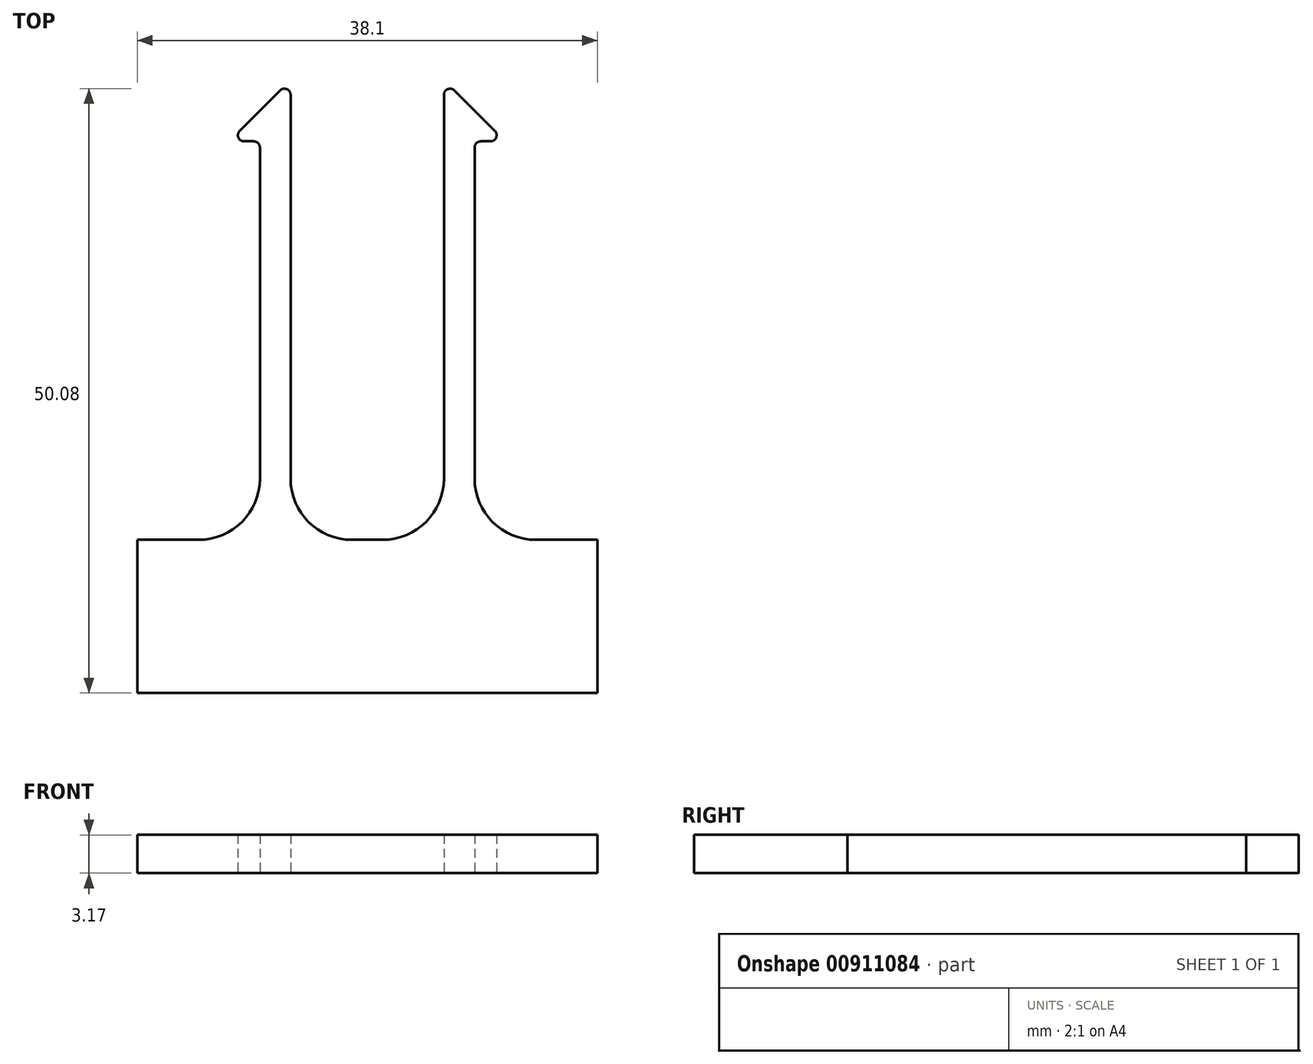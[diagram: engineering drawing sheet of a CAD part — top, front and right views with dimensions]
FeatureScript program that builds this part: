
annotation { "Feature Type Name" : "Feature", "Feature Type Description" : "" }
export const myFeature = defineFeature(function(context is Context, id is Id, definition is map)
    precondition{}
    {
        {
            var Q0;
            Q0=qCreatedBy(makeId("Top.planeOp"),FACE);
            var sketch = newSketch(context, id + "F0", { "sketchPlane" : qUnion([Q0])});
            skLineSegment(sketch, "E0.bottom", {"start": v(0, 0) * mm, "end": v(38.1, 0) * mm});
            skLineSegment(sketch, "E0.top", {"start": v(0, 50.8) * mm, "end": v(38.1, 50.8) * mm});
            skLineSegment(sketch, "E0.left", {"start": v(0, 0) * mm, "end": v(0, 50.8) * mm});
            skLineSegment(sketch, "E0.right", {"start": v(38.1, 0) * mm, "end": v(38.1, 50.8) * mm});
            skLineSegment(sketch, "E1", {"start": v(12.7, 50.8) * mm, "end": v(12.7, 12.7) * mm});
            skLineSegment(sketch, "E2", {"start": v(12.7, 12.7) * mm, "end": v(25.4, 12.7) * mm});
            skLineSegment(sketch, "E3", {"start": v(25.4, 12.7) * mm, "end": v(25.4, 50.8) * mm});
            skLineSegment(sketch, "E4", {"start": v(12.7, 50.8) * mm, "end": v(7.62, 45.72) * mm});
            skLineSegment(sketch, "E5", {"start": v(7.62, 45.72) * mm, "end": v(10.16, 45.72) * mm});
            skLineSegment(sketch, "E6", {"start": v(10.16, 45.72) * mm, "end": v(10.16, 12.7) * mm});
            skLineSegment(sketch, "E7", {"start": v(25.4, 50.8) * mm, "end": v(30.48, 45.72) * mm});
            skLineSegment(sketch, "E8", {"start": v(30.48, 45.72) * mm, "end": v(27.94, 45.72) * mm});
            skLineSegment(sketch, "E9", {"start": v(27.94, 45.72) * mm, "end": v(27.94, 12.7) * mm});
            skLineSegment(sketch, "E10", {"start": v(27.94, 12.7) * mm, "end": v(38.1, 12.7) * mm});
            skLineSegment(sketch, "E11", {"start": v(10.16, 12.7) * mm, "end": v(0, 12.7) * mm});
            skSolve(sketch);
        }
        {
            var Q0;
            {var subQ0=sQuery(id+"F0.wireOp",EDGE,"E0.bottom");Q0=makeQuery(id+"F0.imprint","IMPRINT",FACE,{"disambiguationData":[TD([[makeQuery(id+"F0.imprint","IMPRINT",EDGE,{"derivedFrom":subQ0}),1.0]])]});}
            extrude(context, id + "F1", {"entities" : qUnion([Q0]), "depth" : 3.17 * mm, "offsetDistance" : 25.4 * mm});
        }
        {
            var Q0;
            Q0=makeQuery(id+"F1.opExtrude","SWEPT_EDGE",EDGE,{"disambiguationData":[OSD([sQuery(id+"F0.wireOp",EDGE,"E9"),sQuery(id+"F0.wireOp",EDGE,"E10")])]});
            var Q1;
            Q1=makeQuery(id+"F1.opExtrude","SWEPT_EDGE",EDGE,{"disambiguationData":[OSD([sQuery(id+"F0.wireOp",EDGE,"E2"),sQuery(id+"F0.wireOp",EDGE,"E3")])]});
            var Q2;
            Q2=makeQuery(id+"F1.opExtrude","SWEPT_EDGE",EDGE,{"disambiguationData":[OSD([sQuery(id+"F0.wireOp",EDGE,"E1"),sQuery(id+"F0.wireOp",EDGE,"E2")])]});
            var Q3;
            Q3=makeQuery(id+"F1.opExtrude","SWEPT_EDGE",EDGE,{"disambiguationData":[OSD([sQuery(id+"F0.wireOp",EDGE,"E6"),sQuery(id+"F0.wireOp",EDGE,"E11")])]});
            fillet(context, id + "F2", {"entities" : qUnion([Q0, Q1, Q2, Q3]), "radius" : 5.08 * mm, "tangentPropagation" : true, "allowEdgeOverflow" : false});
        }
        {
            var Q0;
            Q0=makeQuery(id+"F1.opExtrude","SWEPT_EDGE",EDGE,{"disambiguationData":[OSD([sQuery(id+"F0.wireOp",EDGE,"E8"),sQuery(id+"F0.wireOp",EDGE,"E9")])]});
            var Q1;
            Q1=makeQuery(id+"F1.opExtrude","SWEPT_EDGE",EDGE,{"disambiguationData":[OSD([sQuery(id+"F0.wireOp",EDGE,"E7"),sQuery(id+"F0.wireOp",EDGE,"E8")])]});
            var Q2;
            Q2=makeQuery(id+"F1.opExtrude","SWEPT_EDGE",EDGE,{"disambiguationData":[OSD([sQuery(id+"F0.wireOp",EDGE,"E5"),sQuery(id+"F0.wireOp",EDGE,"E6")])]});
            var Q3;
            Q3=makeQuery(id+"F1.opExtrude","SWEPT_EDGE",EDGE,{"disambiguationData":[OSD([sQuery(id+"F0.wireOp",EDGE,"E4"),sQuery(id+"F0.wireOp",EDGE,"E5")])]});
            var Q4;
            Q4=makeQuery(id+"F1.opExtrude","SWEPT_EDGE",EDGE,{"disambiguationData":[OSD([sQuery(id+"F0.wireOp",EDGE,"E0.top"),sQuery(id+"F0.wireOp",EDGE,"E1"),sQuery(id+"F0.wireOp",EDGE,"E4")])]});
            var Q5;
            Q5=makeQuery(id+"F1.opExtrude","SWEPT_EDGE",EDGE,{"disambiguationData":[OSD([sQuery(id+"F0.wireOp",EDGE,"E0.top"),sQuery(id+"F0.wireOp",EDGE,"E3"),sQuery(id+"F0.wireOp",EDGE,"E7")])]});
            fillet(context, id + "F3", {"entities" : qUnion([Q0, Q1, Q2, Q3, Q4, Q5]), "radius" : 0.5 * mm, "tangentPropagation" : true, "allowEdgeOverflow" : false});
        }
    });
